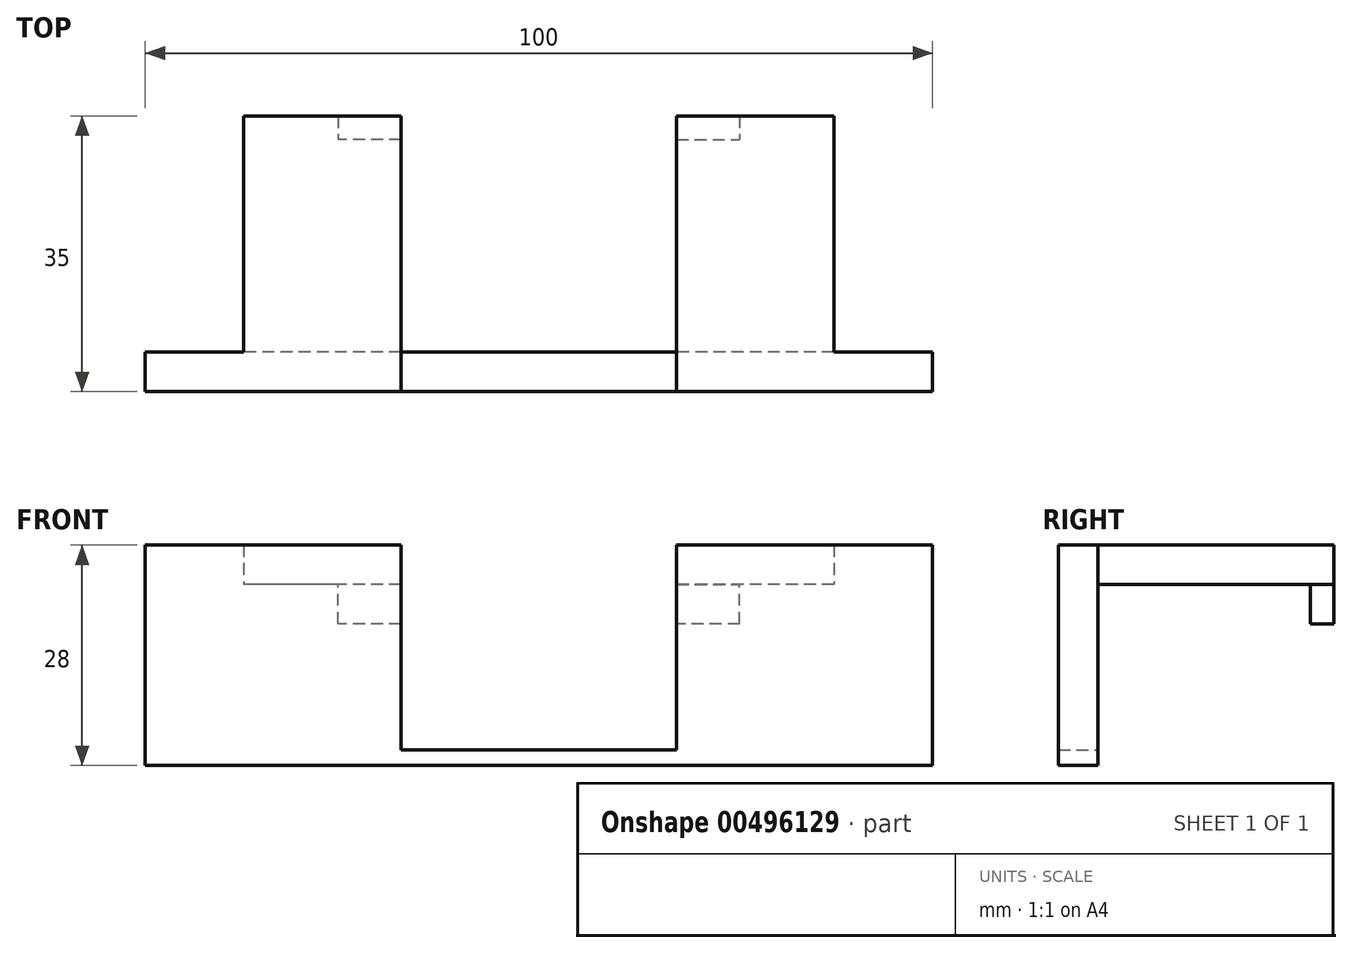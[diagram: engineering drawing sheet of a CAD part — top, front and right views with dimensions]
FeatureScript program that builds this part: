
annotation { "Feature Type Name" : "Feature", "Feature Type Description" : "" }
export const myFeature = defineFeature(function(context is Context, id is Id, definition is map)
    precondition{}
    {
        {
            var Q0;
            Q0=qCreatedBy(makeId("Front.planeOp"),FACE);
            var sketch = newSketch(context, id + "F0", { "sketchPlane" : qUnion([Q0])});
            skLineSegment(sketch, "E0.bottom", {"start": v(-50, -14) * mm, "end": v(50, -14) * mm});
            skLineSegment(sketch, "E0.top", {"start": v(-50, 14) * mm, "end": v(50, 14) * mm});
            skLineSegment(sketch, "E0.left", {"start": v(-50, -14) * mm, "end": v(-50, 14) * mm});
            skLineSegment(sketch, "E0.right", {"start": v(50, -14) * mm, "end": v(50, 14) * mm});
            skPoint(sketch, "E0.middle", {"position": v(0, 0) * mm});
            skLineSegment(sketch, "E1.bottom", {"start": v(17.5, -14) * mm, "end": v(-17.5, -14) * mm});
            skLineSegment(sketch, "E1.top", {"start": v(17.5, 14) * mm, "end": v(-17.5, 14) * mm});
            skSolve(sketch);
        }
        {
            var Q0;
            {var subQ3=sQuery(id+"F0.wireOp",EDGE,"E0.left");Q0=makeQuery(id+"F0.imprint","IMPRINT",FACE,{"disambiguationData":[TD([[makeQuery(id+"F0.imprint","IMPRINT",EDGE,{"derivedFrom":subQ3}),-1.0]])]});}
            var sketch = newSketch(context, id + "F1", { "sketchPlane" : qUnion([Q0])});
            skLineSegment(sketch, "E2.bottom", {"start": v(17.5, -12) * mm, "end": v(-17.5, -12) * mm});
            skLineSegment(sketch, "E2.top", {"start": v(17.5, 14) * mm, "end": v(-17.5, 14) * mm});
            skLineSegment(sketch, "E2.left", {"start": v(17.5, -12) * mm, "end": v(17.5, 14) * mm});
            skLineSegment(sketch, "E2.right", {"start": v(-17.5, -12) * mm, "end": v(-17.5, 14) * mm});
            skPoint(sketch, "E2.middle", {"position": v(0, 1) * mm});
            skSolve(sketch);
        }
        {
            var Q0;
            Q0 = qSketchRegion(id + "F0", true);
            extrude(context, id + "F2", {"entities" : qUnion([Q0]), "depth" : 5 * mm});
        }
        {
            var Q0;
            Q0 = qSketchRegion(id + "F1", true);
            extrude(context, id + "F3", {"entities" : qUnion([Q0]), "operationType" : NewBodyOperationType.REMOVE, "depth" : 25.4 * mm});
        }
        {
            var Q0;
            Q0=qCreatedBy(makeId("Front.planeOp"),FACE);
            var sketch = newSketch(context, id + "F4", { "sketchPlane" : qUnion([Q0])});
            skLineSegment(sketch, "E3.bottom", {"start": v(-17.5, 14) * mm, "end": v(-37.5, 14) * mm});
            skLineSegment(sketch, "E3.top", {"start": v(-17.5, 9) * mm, "end": v(-37.5, 9) * mm});
            skLineSegment(sketch, "E3.left", {"start": v(-17.5, 14) * mm, "end": v(-17.5, 9) * mm});
            skLineSegment(sketch, "E3.right", {"start": v(-37.5, 14) * mm, "end": v(-37.5, 9) * mm});
            skLineSegment(sketch, "E4.bottom", {"start": v(37.5, 14) * mm, "end": v(17.5, 14) * mm});
            skLineSegment(sketch, "E4.top", {"start": v(37.5, 9) * mm, "end": v(17.5, 9) * mm});
            skLineSegment(sketch, "E4.left", {"start": v(37.5, 14) * mm, "end": v(37.5, 9) * mm});
            skLineSegment(sketch, "E4.right", {"start": v(17.5, 14) * mm, "end": v(17.5, 9) * mm});
            skSolve(sketch);
        }
        {
            var Q0;
            Q0 = qSketchRegion(id + "F4", true);
            extrude(context, id + "F5", {"entities" : qUnion([Q0]), "operationType" : NewBodyOperationType.ADD, "oppositeDirection" : true, "depth" : 30 * mm});
        }
        {
            var Q0;
            Q0=makeQuery(id+"F5.opExtrude","SWEPT_FACE",FACE,{"disambiguationData":[OSD([sQuery(id+"F4.wireOp",EDGE,"E3.top")])]});
            var sketch = newSketch(context, id + "F6", { "sketchPlane" : qUnion([Q0])});
            skLineSegment(sketch, "E5.bottom", {"start": v(-17.5, -30) * mm, "end": v(-25.5, -30) * mm});
            skLineSegment(sketch, "E5.top", {"start": v(-17.5, -27) * mm, "end": v(-25.5, -27) * mm});
            skLineSegment(sketch, "E5.left", {"start": v(-17.5, -30) * mm, "end": v(-17.5, -27) * mm});
            skLineSegment(sketch, "E5.right", {"start": v(-25.5, -30) * mm, "end": v(-25.5, -27) * mm});
            skSolve(sketch);
        }
        {
            var Q0;
            Q0=makeQuery(id+"F5.opExtrude","SWEPT_FACE",FACE,{"disambiguationData":[OSD([sQuery(id+"F4.wireOp",EDGE,"E4.top")])]});
            var sketch = newSketch(context, id + "F7", { "sketchPlane" : qUnion([Q0])});
            skLineSegment(sketch, "E6.bottom", {"start": v(17.5, -30) * mm, "end": v(25.5, -30) * mm});
            skLineSegment(sketch, "E6.top", {"start": v(17.5, -27) * mm, "end": v(25.5, -27) * mm});
            skLineSegment(sketch, "E6.left", {"start": v(17.5, -30) * mm, "end": v(17.5, -27) * mm});
            skLineSegment(sketch, "E6.right", {"start": v(25.5, -30) * mm, "end": v(25.5, -27) * mm});
            skSolve(sketch);
        }
        {
            var Q0;
            Q0 = qSketchRegion(id + "F6", true);
            var Q1;
            Q1 = qSketchRegion(id + "F7", true);
            extrude(context, id + "F8", {"entities" : qUnion([Q0, Q1]), "operationType" : NewBodyOperationType.ADD, "depth" : 5 * mm});
        }
    });
